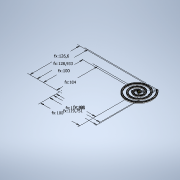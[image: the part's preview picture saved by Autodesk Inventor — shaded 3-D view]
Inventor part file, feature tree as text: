
AUTODESK INVENTOR PART (.ipt)
format: ipt  version: 2022.2 (Build 262287000, 287)  size: 743,936 bytes
history: native  units: mm
features: other x4, extrude x2, fillet x1, sketch x1, projected_geometry x1
ambient origin geometry x8: Origin, YZ Plane, XZ Plane, XY Plane, X Axis, Y Axis, Z Axis, Center Point
bodies: Body1 (feature_tree)
feature tree (9):
  other  "Rotor Wrap"
  other  "Rotor Profile"
  extrude  "Rotor Wrap Extrusion"  Depth=0.45mm
  extrude  "Extrusion5"  Depth=0.45mm
  fillet  "Fillet2"  Radius=100.0mm
  other  "rotor_outer"
  other  "rotor_inner"
  sketch  "Sketch7"  dims[d0=0.0mm d1=213.1131mm d2=100.0mm d3=100.0mm d4=119.751226mm d5=128.93306mm d8=0.0mm d9=181.697174mm d10=117.865222mm d11=126.600039mm d22=3.0mm d23=0.0mm d24=104.0mm d27=4.0mm d28=100.0mm d195=0.0mm d46=181.697174mm d50=0.0mm d51=213.1131mm d72=100.0mm d73=100.0mm d74=78.951679mm d78=98.0mm d79=100.0mm d82=73.06694mm d83=104.0mm d84=96.816901mm d87=1.5mm d98=5.844343mm d99=1.844343mm d100=9.746017mm d101=0.0mm d253=0.0mm d254=4.0mm d258=0.8mm d259=0.0mm d265=1.0mm d266=0.5mm d267=0.3mm d45=1.844343mm d47=5.844343mm d52=0.95mm d53=1.0mm d54=1.0mm d55=0.0mm d56=0.45mm]
  projected_geometry  "Projected Loop3"
